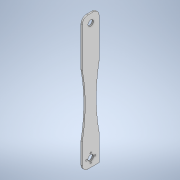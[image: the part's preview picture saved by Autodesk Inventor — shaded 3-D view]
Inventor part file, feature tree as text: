
AUTODESK INVENTOR PART (.ipt)
format: ipt  version: 2020 (Build 240168000, 168)  size: 154,624 bytes
history: native  units: in
note: dims shown in document units (in); Inventor stores cm internally (conversion verified against a paired STEP export)
features: extrude x3, sketch x3, fillet x2
ambient origin geometry x8: Origin, YZ Plane, XZ Plane, XY Plane, X Axis, Y Axis, Z Axis, Center Point
bodies: Solid1 (feature_tree)
feature tree (8):
  extrude  "Extrusion1"  TaperAngle=90.0deg  [1 undecoded]
  extrude  "Extrusion2"  Depth=0.128in TaperAngle=0.0deg
  fillet  "Fillet1"  Radius=0.75in
  fillet  "Fillet2"  Radius=0.5in
  extrude  "Extrusion3"  Depth=15.0in
  sketch  "Sketch1"  dims[d0=1.5in d1=90.0deg]
  sketch  "Sketch2"  dims[d2=12.0in d3=0.128in d4=0.0in d5=0.75in d6=0.5in]
  sketch  "Sketch3"  dims[d7=0.385in d8=0.77in d9=0.14in d10=0.14in d11=0.385in d12=0.77in d13=0.14in d14=0.14in d15=1.0in d16=0.0in d17=0.75in d18=0.5in d19=0.5in d20=0.5in d21=15.0in d22=15.0in d23=2.4375in d24=0.0in]
note: 1 required parameter value undecoded (feature->parameter linkage not recoverable at this tier; creation-order binding heuristic only, values carry confidence <= 0.55)
